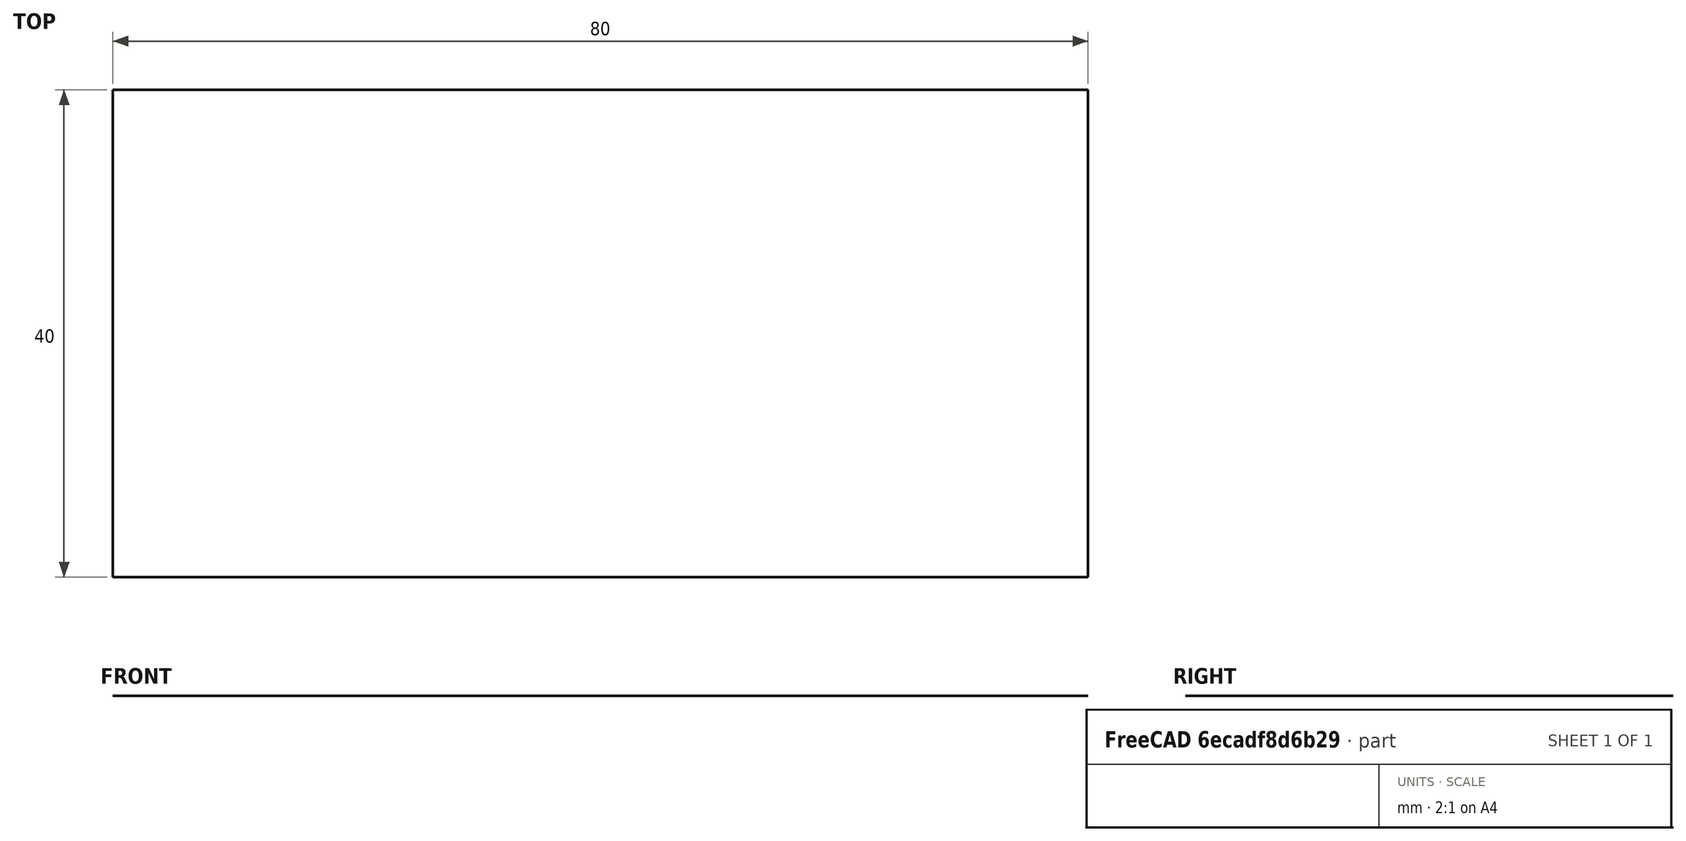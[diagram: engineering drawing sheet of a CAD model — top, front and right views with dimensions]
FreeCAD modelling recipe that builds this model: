
FCSTD DOCUMENT  (FreeCAD 0.16R6712 (Git))
Label: Drill_Marking_G366
License: All rights reserved
LicenseURL: http://en.wikipedia.org/wiki/All_rights_reserved
objects: Drawing::FeatureViewPython×14, Part::Part2DObjectPython×4, Part::MultiFuse×1, Drawing::FeatureViewPart×1, Drawing::FeaturePage×1
note: 5 computed .brp shape members not serialized (recipe doc carries the construction recipe); baked Part::Feature solids carry a one-line shape summary decoded from their .brp

FEATURE [Part::Part2DObjectPython] Rectangle  # Draft 2D object (typed FeaturePython)
  ChamferSize = 0
  Columns = 1
  FilletRadius = 0
  Height = 40
  Length = 80
  MakeFace = true
  Rows = 1
FEATURE [Part::Part2DObjectPython] Circle  # Draft 2D object (typed FeaturePython)
  FirstAngle = 0
  LastAngle = 0
  MakeFace = true
  Placement = pos=(40,28,0) rot=(0.707107,0.707107,0;3.14159rad)
  Radius = 6
FEATURE [Part::Part2DObjectPython] Circle001  # Draft 2D object (typed FeaturePython)
  FirstAngle = 0
  LastAngle = 0
  MakeFace = true
  Placement = pos=(30,10,0) rot=(0.707107,0.707107,0;3.14159rad)
  Radius = 5
FEATURE [Part::Part2DObjectPython] Circle002  # Draft 2D object (typed FeaturePython)
  FirstAngle = 0
  LastAngle = 0
  MakeFace = true
  Placement = pos=(50,10,0) rot=(0,0,1;0rad)
  Radius = 6
  Support = -> Rectangle
FEATURE [Part::MultiFuse] Fusion
  Shapes = -> [Rectangle,Circle002,Circle001,Circle]
FEATURE [Drawing::FeatureViewPart] View001
  Direction = (0,0,1)
  HiddenWidth = 0.15
  LineWidth = 0.35
  Rotation = 0
  ShowHiddenLines = false
  ShowSmoothLines = false
  Source = -> Fusion
  Tolerance = 0.05
  ViewResult = <g id="View001"\n   transform="rotate(0,100,100) translate(100,100) scale(1,1)"\n  >\n<g   stroke="rgb(0, 0, 0)"\n   stroke-width="0.35"\n   stroke-linecap="butt"\n   stroke-linejoin="miter"\n   fill="none"\n   transform="scale(1,-1)"\n  >\n<circle cx ="40" cy ="28" r ="6" /><path id= "2" d=" M 0 0 L 80 2.44929e-015 " />\n<path id= "3" d=" M -1.22465e-015 40 L 0 0 " />\n<path id= "4" d=" M 80 2.44929e-015 L 80 40 " />\n<path id= "5" d=" M 80 40 L 0 40 " />\n<circle cx ="50" cy ="10" r ="6" /><circle cx ="30" cy ="10" r ="5" /></g>\n</g>
  Visible = true
  X = 100
  Y = 100
FEATURE [Drawing::FeatureViewPython] dim001  # drawing view (typed FeaturePython)
  Rotation = 0
  ViewResult = <g> \n  <line x1="180.000000" y1="58.000000" x2="180.000000" y2="49.000000" style="stroke:rgb(0,0,255);stroke-width:0.50" />\n<line x1="100.000000" y1="58.000000" x2="100.000000" y2="49.000000" style="stroke:rgb(0,0,255);stroke-width:0.50" />\n<line x1="180.000000" y1="50.000000" x2="100.000000" y2="50.000000" style="stroke:rgb(0,0,255);stroke-width:0.50" /> \n  <polygon points="100.000000,50.000000 103.000000,51.000000 104.000000,50.000000 103.000000,49.000000" style="fill:rgb(0,0,255);stroke:rgb(0,0,255);stroke-width:0" /><polygon points="180.000000,50.000000 177.000000,49.000000 176.000000,50.000000 177.000000,51.000000" style="fill:rgb(0,0,255);stroke:rgb(0,0,255);stroke-width:0" /> \n  <text x="140.000000" y="48.000000" font-family="inherit" font-size="3.6" fill="rgb(0,0,255)" text-anchor="middle" transform="rotate(0.000000 140.000000,48.000000)" >80</text> </g>
  Visible = true
  X = 0
  Y = 0
  arrowL1 = 3
  arrowL2 = 1
  arrowW = 2
  arrow_scheme = 0
  autoPlaceOffset = 2
  autoPlaceText = true
  click1_x = 140
  click1_y = 50
  click2_x = 140
  click2_y = 50
  comma_decimal_place = false
  dimension_line_overshoot = 1
  gap_datum_points = 2
  halfDimension_linear = false
  lineColor = rgb(0,0,255)
  strokeWidth = 0.5
  textFormat_linear = %(value)3.3f
  textRenderer_color = rgb(0,0,255)
  textRenderer_family = inherit
  textRenderer_size = 3.6
  unit_custom_scale = 1
  unit_scheme = 0
FEATURE [Drawing::FeatureViewPython] dim002  # drawing view (typed FeaturePython)
  Rotation = 0
  ViewResult = <g> \n  <line x1="182.000000" y1="100.000000" x2="191.000000" y2="100.000000" style="stroke:rgb(0,0,255);stroke-width:0.50" />\n<line x1="182.000000" y1="60.000000" x2="191.000000" y2="60.000000" style="stroke:rgb(0,0,255);stroke-width:0.50" />\n<line x1="190.000000" y1="100.000000" x2="190.000000" y2="60.000000" style="stroke:rgb(0,0,255);stroke-width:0.50" /> \n  <polygon points="190.000000,60.000000 189.000000,63.000000 190.000000,64.000000 191.000000,63.000000" style="fill:rgb(0,0,255);stroke:rgb(0,0,255);stroke-width:0" /><polygon points="190.000000,100.000000 191.000000,97.000000 190.000000,96.000000 189.000000,97.000000" style="fill:rgb(0,0,255);stroke:rgb(0,0,255);stroke-width:0" /> \n  <text x="188.000000" y="80.000000" font-family="inherit" font-size="3.6" fill="rgb(0,0,255)" text-anchor="middle" transform="rotate(-90.000000 188.000000,80.000000)" >40</text> </g>
  Visible = true
  X = 0
  Y = 0
  arrowL1 = 3
  arrowL2 = 1
  arrowW = 2
  arrow_scheme = 0
  autoPlaceOffset = 2
  autoPlaceText = true
  click1_x = 190
  click1_y = 70
  click2_x = 190
  click2_y = 70
  comma_decimal_place = false
  dimension_line_overshoot = 1
  gap_datum_points = 2
  halfDimension_linear = false
  lineColor = rgb(0,0,255)
  strokeWidth = 0.5
  textFormat_linear = %(value)3.3f
  textRenderer_color = rgb(0,0,255)
  textRenderer_family = inherit
  textRenderer_size = 3.6
  unit_custom_scale = 1
  unit_scheme = 0
FEATURE [Drawing::FeatureViewPython] centerLines001  # drawing view (typed FeaturePython)
  Rotation = 0
  ViewResult = <g transform="scale(1.000000,1.000000)" stroke="rgb(0,0,255)"  stroke-width="0.320000" > <path d="M 140.000000,72.000000 L 140.000000,69.000000 M 140.000000,67.000000 L 140.000000,61.000000 "/>\n<path d="M 140.000000,72.000000 L 143.000000,72.000000 M 145.000000,72.000000 L 150.000000,72.000000 "/>\n<path d="M 140.000000,72.000000 L 140.000000,75.000000 M 140.000000,77.000000 L 140.000000,80.000000 "/>\n<path d="M 140.000000,72.000000 L 137.000000,72.000000 M 135.000000,72.000000 L 130.000000,72.000000 "/> </g> 
  Visible = true
  X = 0
  Y = 0
  centerLine_color = rgb(0,0,255)
  centerLine_len_dash = 6
  centerLine_len_dot = 3
  centerLine_len_gap = 2
  centerLine_width = 0.32
  click1_x = 150
  click1_y = 60
  click2_x = 130
  click2_y = 80
FEATURE [Drawing::FeatureViewPython] centerLines002  # drawing view (typed FeaturePython)
  Rotation = 0
  ViewResult = <g transform="scale(1.000000,1.000000)" stroke="rgb(0,0,255)"  stroke-width="0.320000" > <path d="M 130.000000,90.000000 L 130.000000,87.000000 M 130.000000,85.000000 L 130.000000,80.000000 "/>\n<path d="M 130.000000,90.000000 L 127.000000,90.000000 M 125.000000,90.000000 L 120.000000,90.000000 "/>\n<path d="M 130.000000,90.000000 L 130.000000,93.000000 M 130.000000,95.000000 L 130.000000,100.000000 "/>\n<path d="M 130.000000,90.000000 L 133.000000,90.000000 M 135.000000,90.000000 L 140.000000,90.000000 "/> </g> 
  Visible = true
  X = 0
  Y = 0
  centerLine_color = rgb(0,0,255)
  centerLine_len_dash = 6
  centerLine_len_dot = 3
  centerLine_len_gap = 2
  centerLine_width = 0.32
  click1_x = 120
  click1_y = 80
  click2_x = 140
  click2_y = 100
FEATURE [Drawing::FeatureViewPython] centerLines003  # drawing view (typed FeaturePython)
  Rotation = 0
  ViewResult = <g transform="scale(1.000000,1.000000)" stroke="rgb(0,0,255)"  stroke-width="0.320000" > <path d="M 150.000000,90.000000 L 150.000000,93.000000 M 150.000000,95.000000 L 150.000000,100.000000 "/>\n<path d="M 150.000000,90.000000 L 153.000000,90.000000 M 155.000000,90.000000 L 160.000000,90.000000 "/>\n<path d="M 150.000000,90.000000 L 150.000000,87.000000 M 150.000000,85.000000 L 150.000000,80.000000 "/>\n<path d="M 150.000000,90.000000 L 147.000000,90.000000 M 145.000000,90.000000 L 140.000000,90.000000 "/> </g> 
  Visible = true
  X = 0
  Y = 0
  centerLine_color = rgb(0,0,255)
  centerLine_len_dash = 6
  centerLine_len_dot = 3
  centerLine_len_gap = 2
  centerLine_width = 0.32
  click1_x = 160
  click1_y = 100
  click2_x = 140
  click2_y = 80
FEATURE [Drawing::FeatureViewPython] dia001  # drawing view (typed FeaturePython)
  Rotation = 0
  ViewResult = <g>  <circle cx ="140.000000" cy ="72.000000" r="0.250000" stroke="none" fill="rgb(0,0,255)" /> \n<line x1="150.000000" y1="65.000000" x2="135.084608" y2="75.440774" style="stroke:rgb(0,0,255);stroke-width:0.50" />\n<polygon points="144.915392,68.559226 141.884233,69.460381 141.638464,70.853075 143.031158,71.098845" style="fill:rgb(0,0,255);stroke:rgb(0,0,255);stroke-width:0" />\n<polygon points="135.084608,75.440774 138.115767,74.539619 138.361536,73.146925 136.968842,72.901155" style="fill:rgb(0,0,255);stroke:rgb(0,0,255);stroke-width:0" />\n<line x1="150.000000" y1="65.000000" x2="165.000000" y2="65.000000" style="stroke:rgb(0,0,255);stroke-width:0.50" />\n<text x="157.500000" y="63.000000" font-family="inherit" font-size="3.6" fill="rgb(0,0,255)" text-anchor="middle" transform="rotate(0.000000 157.500000,63.000000)" >Ø12</text> </g>
  Visible = true
  X = 0
  Y = 0
  arrowL1 = 3
  arrowL2 = 1
  arrowW = 2
  arrow_scheme = 0
  autoPlaceOffset = 2
  autoPlaceText = true
  centerPointDia = 0.5
  click1_x = 150
  click1_y = 65
  click2_x = 165
  click2_y = 65
  click3_x = 165
  click3_y = 65
  comma_decimal_place = false
  lineColor = rgb(0,0,255)
  strokeWidth = 0.5
  textFormat_circular = Ø%(value)3.3f
  textRenderer_color = rgb(0,0,255)
  textRenderer_family = inherit
  textRenderer_size = 3.6
  unit_custom_scale = 1
  unit_scheme = 0
FEATURE [Drawing::FeatureViewPython] dia002  # drawing view (typed FeaturePython)
  Rotation = 0
  ViewResult = <g>  <circle cx ="150.000000" cy ="90.000000" r="0.250000" stroke="none" fill="rgb(0,0,255)" /> \n<line x1="160.000000" y1="80.000000" x2="145.757359" y2="94.242641" style="stroke:rgb(0,0,255);stroke-width:0.50" />\n<polygon points="154.242641,85.757359 151.414214,87.171573 151.414214,88.585786 152.828427,88.585786" style="fill:rgb(0,0,255);stroke:rgb(0,0,255);stroke-width:0" />\n<polygon points="145.757359,94.242641 148.585786,92.828427 148.585786,91.414214 147.171573,91.414214" style="fill:rgb(0,0,255);stroke:rgb(0,0,255);stroke-width:0" />\n<line x1="160.000000" y1="80.000000" x2="175.000000" y2="80.000000" style="stroke:rgb(0,0,255);stroke-width:0.50" />\n<text x="167.500000" y="78.000000" font-family="inherit" font-size="3.6" fill="rgb(0,0,255)" text-anchor="middle" transform="rotate(0.000000 167.500000,78.000000)" >Ø12</text> </g>
  Visible = true
  X = 0
  Y = 0
  arrowL1 = 3
  arrowL2 = 1
  arrowW = 2
  arrow_scheme = 0
  autoPlaceOffset = 2
  autoPlaceText = true
  centerPointDia = 0.5
  click1_x = 160
  click1_y = 80
  click2_x = 175
  click2_y = 80
  click3_x = 175
  click3_y = 80
  comma_decimal_place = false
  lineColor = rgb(0,0,255)
  strokeWidth = 0.5
  textFormat_circular = Ø%(value)3.3f
  textRenderer_color = rgb(0,0,255)
  textRenderer_family = inherit
  textRenderer_size = 3.6
  unit_custom_scale = 1
  unit_scheme = 0
FEATURE [Drawing::FeatureViewPython] dia003  # drawing view (typed FeaturePython)
  Rotation = 0
  ViewResult = <g>  <circle cx ="130.000000" cy ="90.000000" r="0.250000" stroke="none" fill="rgb(0,0,255)" /> \n<line x1="120.000000" y1="80.000000" x2="133.535534" y2="93.535534" style="stroke:rgb(0,0,255);stroke-width:0.50" />\n<polygon points="126.464466,86.464466 127.878680,89.292893 129.292893,89.292893 129.292893,87.878680" style="fill:rgb(0,0,255);stroke:rgb(0,0,255);stroke-width:0" />\n<polygon points="133.535534,93.535534 132.121320,90.707107 130.707107,90.707107 130.707107,92.121320" style="fill:rgb(0,0,255);stroke:rgb(0,0,255);stroke-width:0" />\n<line x1="120.000000" y1="80.000000" x2="110.000000" y2="80.000000" style="stroke:rgb(0,0,255);stroke-width:0.50" />\n<text x="115.000000" y="78.000000" font-family="inherit" font-size="3.6" fill="rgb(0,0,255)" text-anchor="middle" transform="rotate(0.000000 115.000000,78.000000)" >Ø10</text> </g>
  Visible = true
  X = 0
  Y = 0
  arrowL1 = 3
  arrowL2 = 1
  arrowW = 2
  arrow_scheme = 0
  autoPlaceOffset = 2
  autoPlaceText = true
  centerPointDia = 0.5
  click1_x = 120
  click1_y = 80
  click2_x = 110
  click2_y = 80
  click3_x = 110
  click3_y = 80
  comma_decimal_place = false
  lineColor = rgb(0,0,255)
  strokeWidth = 0.5
  textFormat_circular = Ø%(value)3.3f
  textRenderer_color = rgb(0,0,255)
  textRenderer_family = inherit
  textRenderer_size = 3.6
  unit_custom_scale = 1
  unit_scheme = 0
FEATURE [Drawing::FeatureViewPython] dimStack001  # drawing view (typed FeaturePython)
  Rotation = 0
  ViewResult = <g> <line x1="142.000001" y1="72.000000" x2="211.000000" y2="72.000000" style="stroke:rgb(0,0,255);stroke-width:0.50" />\n<line x1="182.000001" y1="60.000000" x2="211.000000" y2="60.000000" style="stroke:rgb(0,0,255);stroke-width:0.50" />\n<line x1="210.000000" y1="72.000000" x2="210.000000" y2="60.000000" style="stroke:rgb(0,0,255);stroke-width:0.50" />\n<polygon points="210.000000,72.000000 211.000000,69.000000 210.000000,68.000000 209.000000,69.000000" style="fill:rgb(0,0,255);stroke:rgb(0,0,255);stroke-width:0" />\n<polygon points="210.000000,60.000000 209.000000,63.000000 210.000000,64.000000 211.000000,63.000000" style="fill:rgb(0,0,255);stroke:rgb(0,0,255);stroke-width:0" />\n<text x="208.000000" y="66.000000" font-family="inherit" font-size="3.6" fill="rgb(0,0,255)" text-anchor="middle" transform="rotate(-90.000000 208.000000,66.000000)" >12</text> </g> 
  Visible = true
  X = 0
  Y = 0
  arrowL1 = 3
  arrowL2 = 1
  arrowW = 2
  arrow_scheme = 0
  autoPlaceOffset = 2
  click1_x = 210
  click1_y = 60
  comma_decimal_place = false
  dimension_line_overshoot = 1
  gap_datum_points = 2
  lineColor = rgb(0,0,255)
  stack_offset = 7
  stack_offset0 = 0
  strokeWidth = 0.5
  textFormat_linear = %(value)3.3f
  textRenderer_color = rgb(0,0,255)
  textRenderer_family = inherit
  textRenderer_size = 3.6
  unit_custom_scale = 1
  unit_scheme = 0
FEATURE [Drawing::FeatureViewPython] dimStack002  # drawing view (typed FeaturePython)
  Rotation = 0
  ViewResult = <g> <line x1="152.000001" y1="90.000000" x2="201.000000" y2="90.000000" style="stroke:rgb(0,0,255);stroke-width:0.50" />\n<line x1="182.000001" y1="60.000000" x2="201.000000" y2="60.000000" style="stroke:rgb(0,0,255);stroke-width:0.50" />\n<line x1="200.000000" y1="90.000000" x2="200.000000" y2="60.000000" style="stroke:rgb(0,0,255);stroke-width:0.50" />\n<polygon points="200.000000,90.000000 201.000000,87.000000 200.000000,86.000000 199.000000,87.000000" style="fill:rgb(0,0,255);stroke:rgb(0,0,255);stroke-width:0" />\n<polygon points="200.000000,60.000000 199.000000,63.000000 200.000000,64.000000 201.000000,63.000000" style="fill:rgb(0,0,255);stroke:rgb(0,0,255);stroke-width:0" />\n<text x="198.000000" y="75.000000" font-family="inherit" font-size="3.6" fill="rgb(0,0,255)" text-anchor="middle" transform="rotate(-90.000000 198.000000,75.000000)" >30</text> </g> 
  Visible = true
  X = 0
  Y = 0
  arrowL1 = 3
  arrowL2 = 1
  arrowW = 2
  arrow_scheme = 0
  autoPlaceOffset = 2
  click1_x = 200
  click1_y = 80
  comma_decimal_place = false
  dimension_line_overshoot = 1
  gap_datum_points = 2
  lineColor = rgb(0,0,255)
  stack_offset = 7
  stack_offset0 = 0
  strokeWidth = 0.5
  textFormat_linear = %(value)3.3f
  textRenderer_color = rgb(0,0,255)
  textRenderer_family = inherit
  textRenderer_size = 3.6
  unit_custom_scale = 1
  unit_scheme = 0
FEATURE [Drawing::FeatureViewPython] dimStack003  # drawing view (typed FeaturePython)
  Rotation = 0
  ViewResult = <g> <line x1="127.999999" y1="90.000000" x2="89.000000" y2="90.000000" style="stroke:rgb(0,0,255);stroke-width:0.50" />\n<line x1="177.999999" y1="60.000000" x2="89.000000" y2="60.000000" style="stroke:rgb(0,0,255);stroke-width:0.50" />\n<line x1="90.000000" y1="90.000000" x2="90.000000" y2="60.000000" style="stroke:rgb(0,0,255);stroke-width:0.50" />\n<polygon points="90.000000,90.000000 91.000000,87.000000 90.000000,86.000000 89.000000,87.000000" style="fill:rgb(0,0,255);stroke:rgb(0,0,255);stroke-width:0" />\n<polygon points="90.000000,60.000000 89.000000,63.000000 90.000000,64.000000 91.000000,63.000000" style="fill:rgb(0,0,255);stroke:rgb(0,0,255);stroke-width:0" />\n<text x="88.000000" y="75.000000" font-family="inherit" font-size="3.6" fill="rgb(0,0,255)" text-anchor="middle" transform="rotate(-90.000000 88.000000,75.000000)" >30</text> </g> 
  Visible = true
  X = 0
  Y = 0
  arrowL1 = 3
  arrowL2 = 1
  arrowW = 2
  arrow_scheme = 0
  autoPlaceOffset = 2
  click1_x = 90
  click1_y = 60
  comma_decimal_place = false
  dimension_line_overshoot = 1
  gap_datum_points = 2
  lineColor = rgb(0,0,255)
  stack_offset = 7
  stack_offset0 = 0
  strokeWidth = 0.5
  textFormat_linear = %(value)3.3f
  textRenderer_color = rgb(0,0,255)
  textRenderer_family = inherit
  textRenderer_size = 3.6
  unit_custom_scale = 1
  unit_scheme = 0
FEATURE [Drawing::FeatureViewPython] dimStack004  # drawing view (typed FeaturePython)
  Rotation = 0
  ViewResult = <g> <line x1="140.000000" y1="69.999999" x2="140.000000" y2="54.000000" style="stroke:rgb(0,0,255);stroke-width:0.50" />\n<line x1="180.000000" y1="57.999999" x2="180.000000" y2="54.000000" style="stroke:rgb(0,0,255);stroke-width:0.50" />\n<line x1="140.000000" y1="55.000000" x2="180.000000" y2="55.000000" style="stroke:rgb(0,0,255);stroke-width:0.50" />\n<polygon points="140.000000,55.000000 143.000000,56.000000 144.000000,55.000000 143.000000,54.000000" style="fill:rgb(0,0,255);stroke:rgb(0,0,255);stroke-width:0" />\n<polygon points="180.000000,55.000000 177.000000,54.000000 176.000000,55.000000 177.000000,56.000000" style="fill:rgb(0,0,255);stroke:rgb(0,0,255);stroke-width:0" />\n<text x="160.000000" y="53.000000" font-family="inherit" font-size="3.6" fill="rgb(0,0,255)" text-anchor="middle" transform="rotate(0.000000 160.000000,53.000000)" >40</text> </g> 
  Visible = true
  X = 0
  Y = 0
  arrowL1 = 3
  arrowL2 = 1
  arrowW = 2
  arrow_scheme = 0
  autoPlaceOffset = 2
  click1_x = 150
  click1_y = 55
  comma_decimal_place = false
  dimension_line_overshoot = 1
  gap_datum_points = 2
  lineColor = rgb(0,0,255)
  stack_offset = 7
  stack_offset0 = 0
  strokeWidth = 0.5
  textFormat_linear = %(value)3.3f
  textRenderer_color = rgb(0,0,255)
  textRenderer_family = inherit
  textRenderer_size = 3.6
  unit_custom_scale = 1
  unit_scheme = 0
FEATURE [Drawing::FeatureViewPython] dimStack005  # drawing view (typed FeaturePython)
  Rotation = 0
  ViewResult = <g> <line x1="130.000000" y1="92.000001" x2="130.000000" y2="106.000000" style="stroke:rgb(0,0,255);stroke-width:0.50" />\n<line x1="180.000000" y1="102.000001" x2="180.000000" y2="106.000000" style="stroke:rgb(0,0,255);stroke-width:0.50" />\n<line x1="130.000000" y1="105.000000" x2="180.000000" y2="105.000000" style="stroke:rgb(0,0,255);stroke-width:0.50" />\n<polygon points="130.000000,105.000000 133.000000,106.000000 134.000000,105.000000 133.000000,104.000000" style="fill:rgb(0,0,255);stroke:rgb(0,0,255);stroke-width:0" />\n<polygon points="180.000000,105.000000 177.000000,104.000000 176.000000,105.000000 177.000000,106.000000" style="fill:rgb(0,0,255);stroke:rgb(0,0,255);stroke-width:0" />\n<text x="155.000000" y="103.000000" font-family="inherit" font-size="3.6" fill="rgb(0,0,255)" text-anchor="middle" transform="rotate(0.000000 155.000000,103.000000)" >50</text> </g> 
  Visible = true
  X = 0
  Y = 0
  arrowL1 = 3
  arrowL2 = 1
  arrowW = 2
  arrow_scheme = 0
  autoPlaceOffset = 2
  click1_x = 140
  click1_y = 105
  comma_decimal_place = false
  dimension_line_overshoot = 1
  gap_datum_points = 2
  lineColor = rgb(0,0,255)
  stack_offset = 7
  stack_offset0 = 0
  strokeWidth = 0.5
  textFormat_linear = %(value)3.3f
  textRenderer_color = rgb(0,0,255)
  textRenderer_family = inherit
  textRenderer_size = 3.6
  unit_custom_scale = 1
  unit_scheme = 0
FEATURE [Drawing::FeatureViewPython] dimStack006  # drawing view (typed FeaturePython)
  Rotation = 0
  ViewResult = <g> <line x1="150.000000" y1="92.000001" x2="150.000000" y2="116.000000" style="stroke:rgb(0,0,255);stroke-width:0.50" />\n<line x1="180.000000" y1="102.000001" x2="180.000000" y2="116.000000" style="stroke:rgb(0,0,255);stroke-width:0.50" />\n<line x1="150.000000" y1="115.000000" x2="180.000000" y2="115.000000" style="stroke:rgb(0,0,255);stroke-width:0.50" />\n<polygon points="150.000000,115.000000 153.000000,116.000000 154.000000,115.000000 153.000000,114.000000" style="fill:rgb(0,0,255);stroke:rgb(0,0,255);stroke-width:0" />\n<polygon points="180.000000,115.000000 177.000000,114.000000 176.000000,115.000000 177.000000,116.000000" style="fill:rgb(0,0,255);stroke:rgb(0,0,255);stroke-width:0" />\n<text x="165.000000" y="113.000000" font-family="inherit" font-size="3.6" fill="rgb(0,0,255)" text-anchor="middle" transform="rotate(0.000000 165.000000,113.000000)" >30</text> </g> 
  Visible = true
  X = 0
  Y = 0
  arrowL1 = 3
  arrowL2 = 1
  arrowW = 2
  arrow_scheme = 0
  autoPlaceOffset = 2
  click1_x = 155
  click1_y = 115
  comma_decimal_place = false
  dimension_line_overshoot = 1
  gap_datum_points = 2
  lineColor = rgb(0,0,255)
  stack_offset = 7
  stack_offset0 = 0
  strokeWidth = 0.5
  textFormat_linear = %(value)3.3f
  textRenderer_color = rgb(0,0,255)
  textRenderer_family = inherit
  textRenderer_size = 3.6
  unit_custom_scale = 1
  unit_scheme = 0
FEATURE [Drawing::FeaturePage] Page
  EditableTexts = Designed by Name | Date | Scale | Weight | Title | Subtitle | Drawing number | Sheet
  Group = -> [View001,dim001,dim002,centerLines001,centerLines002,centerLines003,dia001,dia002,dia003,dimStack001,dimStack002,dimStack003,dimStack004,dimStack005,dimStack006]
